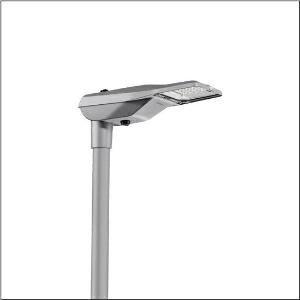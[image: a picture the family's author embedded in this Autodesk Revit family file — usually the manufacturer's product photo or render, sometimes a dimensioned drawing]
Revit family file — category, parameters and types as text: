
# Revit family: streetlight_sl_21_micro___stw1_0a_5xe1e43t08db_d620
name_source: partatom
category: Lighting Fixtures
units: mm (PartAtom-declared; Revit-internal decimal feet)

## family parameters
Cut with Voids When Loaded = No
Host = Face
Light Source = No
Part Type = Normal
Room Calculation Point = No
Round Connector Dimension = Use Diameter
Shared = No

## types (1)
- --- (1 x LED, 5320 lm, 39.1 W, 4000K)
    Apparent Load = 39 VA
    CIE Flux Codes = 38 75 98 100 100
    Color Rendering = 70
    Color Temperature = 4000K
    Default Elevation = 1800 mm
    Description = Streetlight SL 21 micro, mast luminaire, primary light control with lens, of PMMA, primary optical cover: cover, of toughened safety glass, transparent, light distribution: STW1.0a, light emission: direct distribution, primary light characteristic: asymmetric, installation type: side-entry, post-top, LED, High Power LED, rated luminous flux: 5.320lm, luminous efficacy: 136lm/W, light colour: 740, colour temperature: 4000K, control: flexible luminous flux parameterisation, time-dependent luminous flux control, constant luminous flux control, overheat protection, pre-setting: logarithmic dimming characteristic, mains connection: 220..240V, AC, 50/60Hz, start of lifetime: 39W, end of service life: 41W, reduction: 18W, luminaire housing, of diecast aluminium, powder-coated, Siteco® metallic grey (DB 702S), corrosivity category C5 mid according to DIN EN ISO 12944, please order mast flange separately, inclination adjustable: 0°, 5°, 10°, 15°, sealing non-destructively replaceable, multi-level sealing system, length: 528mm, width: 235mm, height: 110mm, mast flange for spigot size: 42mm (side-entry): 5XC10008XM4, 60/48mm (side-entry/post-top): 5XC10108XM2, 76/60mm (side-entry/post-top): 5XC10108XM1, Smart Interface below and above, protection rating (complete): IP66, insulation class (complete): insulation class II (safety insulation), certification: CE, ENEC, ENEC+, VDE, impact resistance: IK09, permissible operating ambient temperature for outdoor applications: -40..+50°C, standard-compliant lighting for roads and squares, packaging unit: 1 piece

Light Distribution: STW1.0a
    Height = 110 mm
    Lamp = 1 x LED
    Lamp Light Flux = 5320 lm
    Lamp Power = 39.1 W
    Lamp count = 1
    Length = 528 mm
    Luminous efficacy = 136 lm/W
    Manufacturer = Siteco
    ModVariant = No
    Model = 5XE1E43T08DB
    Number of Poles = 1
    OnlyDefault = Yes
    Power Factor = 1
    Product Name = Streetlight SL 21 micro | STW1.0a
    Product group = mast luminaire | pylon top
    ProductGroupID = 6100
    Protection Class = Protection class II
    Protection Degree = IP 66
    RLX_Detail_Level = 1
    RLX_Emergency_Light_Flux = 0 lm
    RLX_Emergency_Type = 0
    RLX_Emergency_Type_DB = No
    RlxData = <blob elided: 98201 chars, md5=eba0fcc6>
    Socket = socket
    Standby Power = 0 W
    System Light Flux = 5320 lm
    System Power = 39 W
    Type Comments = factory setting: luminous flux: 100 % | dim-lin: 254 | 765 mA
    Type Image = l_1007239.jpg
    URL = http://relux.com
    VarID = @adj_125605
    Voltage = 0 V
    Weight = 0.00 kg
    Width = 235 mm

## geometry (parser evidence)
native form markers: Blend x4, Sweep x10
no freeform markers — native parametric forms only
